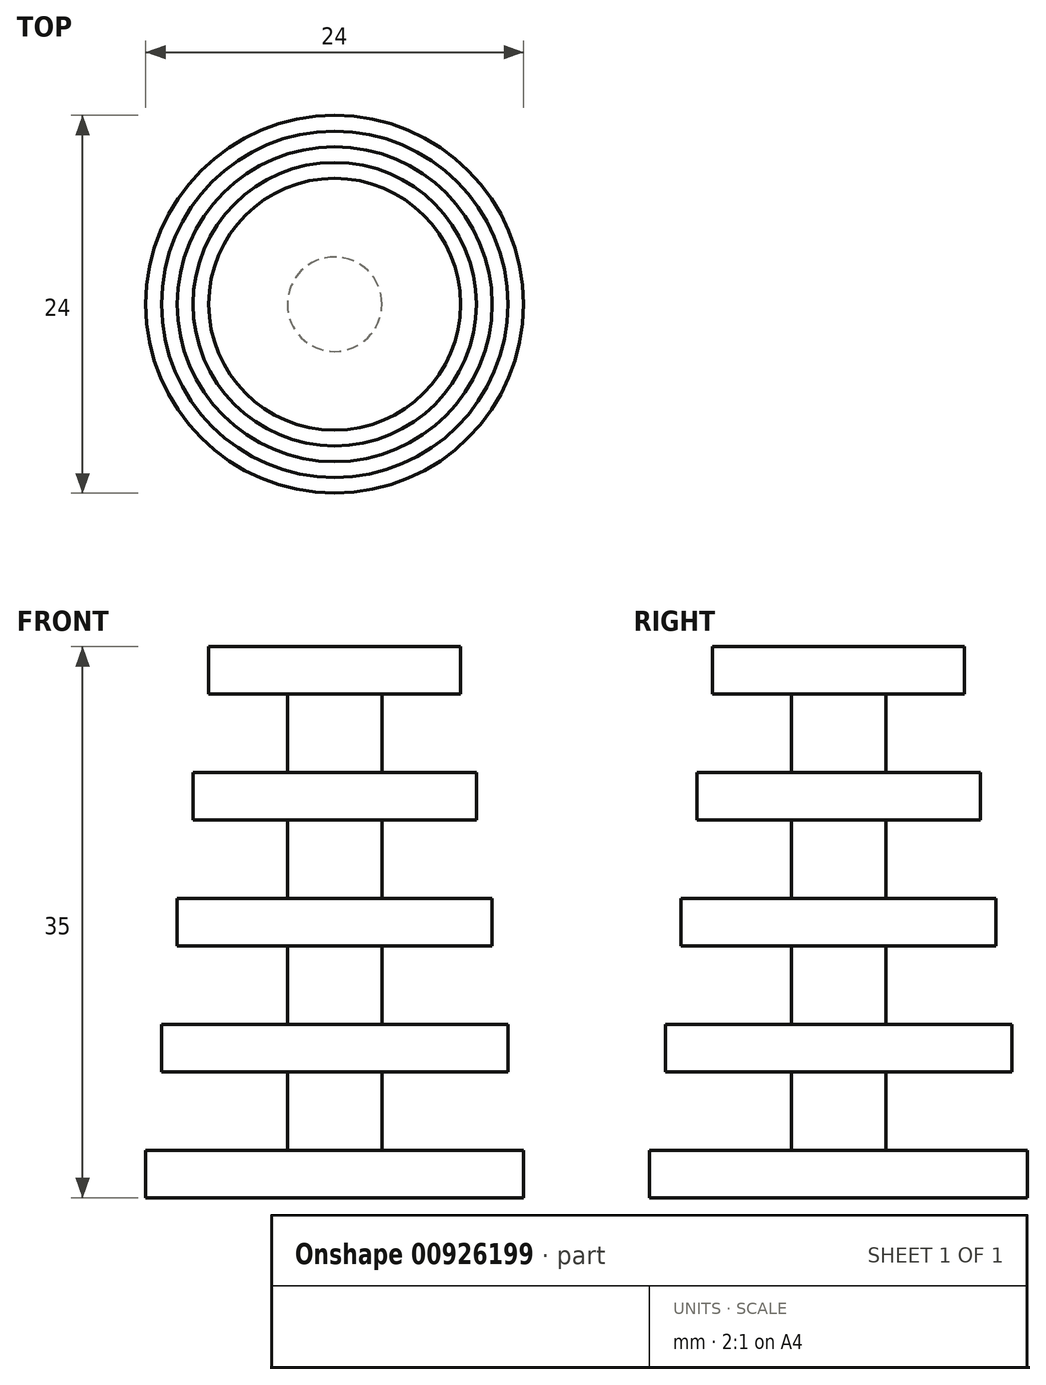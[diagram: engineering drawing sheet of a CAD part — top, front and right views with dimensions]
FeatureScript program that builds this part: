
annotation { "Feature Type Name" : "Feature", "Feature Type Description" : "" }
export const myFeature = defineFeature(function(context is Context, id is Id, definition is map)
    precondition{}
    {
        {
            var Q0;
            Q0=qCreatedBy(makeId("Right.planeOp"),FACE);
            var sketch = newSketch(context, id + "F0", { "sketchPlane" : qUnion([Q0])});
            skLineSegment(sketch, "E0", {"start": v(12, 0) * mm, "end": v(12, 3) * mm});
            skLineSegment(sketch, "E1", {"start": v(12, 3) * mm, "end": v(3, 3) * mm});
            skLineSegment(sketch, "E2", {"start": v(3, 3) * mm, "end": v(3, 8) * mm});
            skLineSegment(sketch, "E3", {"start": v(3, 8) * mm, "end": v(11, 8) * mm});
            skLineSegment(sketch, "E4", {"start": v(11, 8) * mm, "end": v(11, 11) * mm});
            skLineSegment(sketch, "E5", {"start": v(11, 11) * mm, "end": v(3, 11) * mm});
            skLineSegment(sketch, "E6", {"start": v(3, 11) * mm, "end": v(3, 16) * mm});
            skLineSegment(sketch, "E7", {"start": v(3, 16) * mm, "end": v(10, 16) * mm});
            skLineSegment(sketch, "E8", {"start": v(10, 16) * mm, "end": v(10, 19) * mm});
            skLineSegment(sketch, "E9", {"start": v(10, 19) * mm, "end": v(3, 19) * mm});
            skLineSegment(sketch, "E10", {"start": v(3, 19) * mm, "end": v(3, 24) * mm});
            skLineSegment(sketch, "E11", {"start": v(3, 24) * mm, "end": v(9, 24) * mm});
            skLineSegment(sketch, "E12", {"start": v(9, 24) * mm, "end": v(9, 27) * mm});
            skLineSegment(sketch, "E13", {"start": v(9, 27) * mm, "end": v(3, 27) * mm});
            skLineSegment(sketch, "E14", {"start": v(3, 27) * mm, "end": v(3, 32) * mm});
            skLineSegment(sketch, "E15", {"start": v(3, 32) * mm, "end": v(8, 32) * mm});
            skLineSegment(sketch, "E16", {"start": v(8, 32) * mm, "end": v(8, 35) * mm});
            skLineSegment(sketch, "E17", {"start": v(8, 35) * mm, "end": v(0, 35) * mm});
            skLineSegment(sketch, "E18", {"start": v(0, 35) * mm, "end": v(0, 0) * mm});
            skLineSegment(sketch, "E19", {"start": v(12, 0) * mm, "end": v(0, 0) * mm});
            skSolve(sketch);
        }
        {
            var Q0;
            Q0=makeQuery(id+"F0.imprint","IMPRINT",FACE,{"disambiguationData":[TD([[makeQuery(id+"F0.imprint","IMPRINT",EDGE,{"derivedFrom":sQuery(id+"F0.wireOp",EDGE,"E0")}),1.0]])]});
            var Q1;
            Q1=sQuery(id+"F0.wireOp",EDGE,"E18");
            revolve(context, id + "F1", {"surfaceOperationType" : NewSurfaceOperationType.NEW, "entities" : qUnion([Q0]), "axis" : qUnion([Q1]), "revolveType" : RevolveType.FULL});
        }
    });
